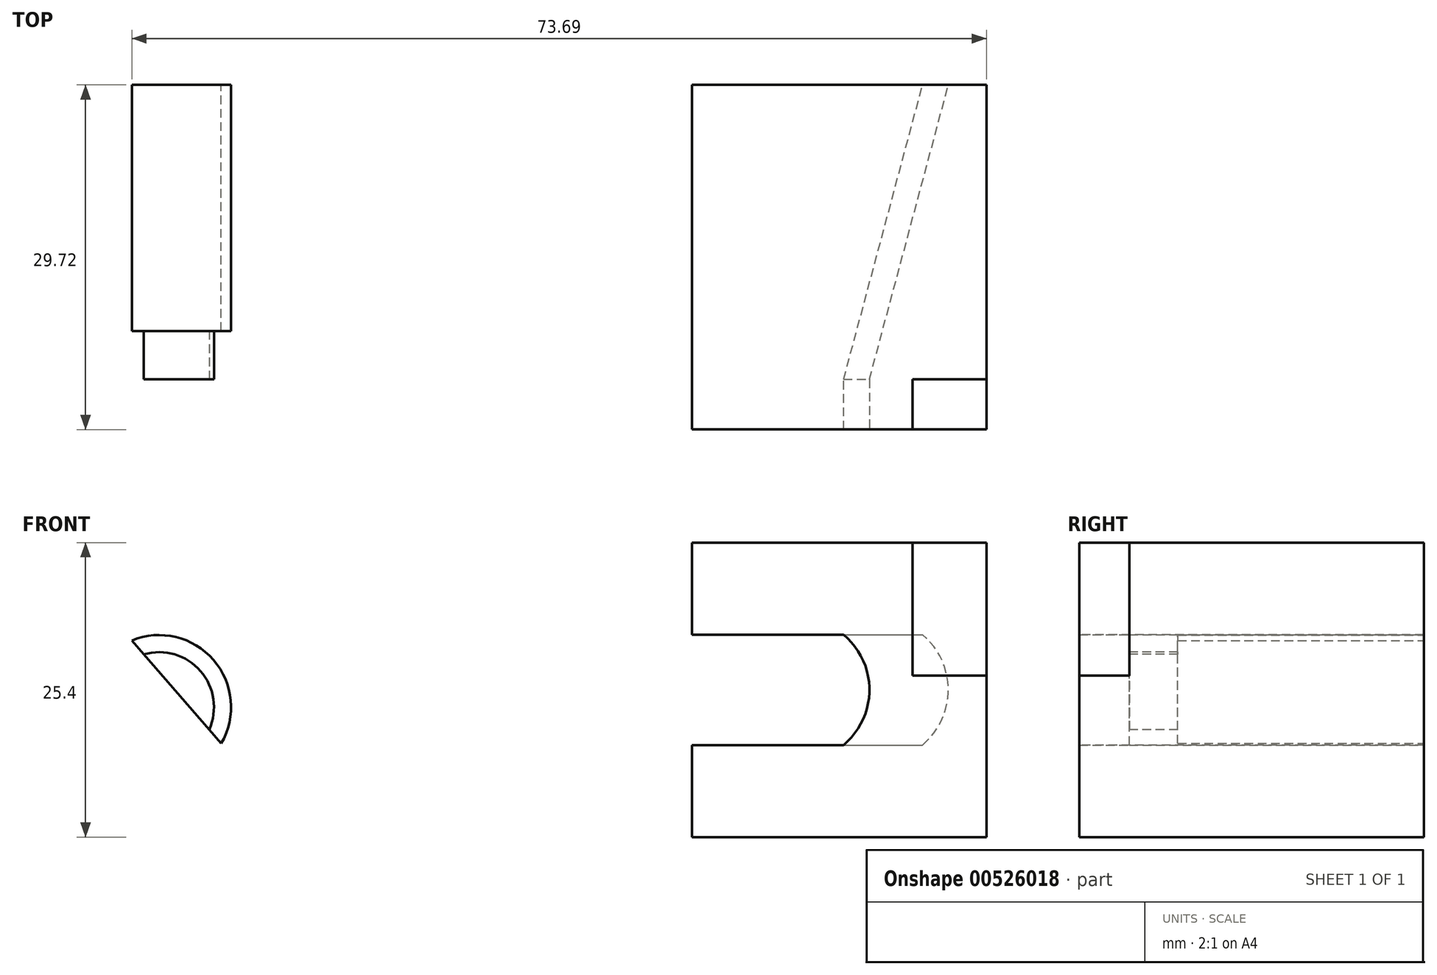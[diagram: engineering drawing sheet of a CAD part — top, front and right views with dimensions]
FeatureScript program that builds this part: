
annotation { "Feature Type Name" : "Feature", "Feature Type Description" : "" }
export const myFeature = defineFeature(function(context is Context, id is Id, definition is map)
    precondition{}
    {
        {
            var Q0;
            Q0=qCreatedBy(makeId("Front.planeOp"),FACE);
            var sketch = newSketch(context, id + "F0", { "sketchPlane" : qUnion([Q0])});
            skLineSegment(sketch, "E0.bottom", {"start": v(0, 0) * mm, "end": v(25.4, 0) * mm});
            skLineSegment(sketch, "E0.top", {"start": v(0, 25.4) * mm, "end": v(25.4, 25.4) * mm});
            skLineSegment(sketch, "E0.left", {"start": v(0, 0) * mm, "end": v(0, 25.4) * mm});
            skLineSegment(sketch, "E0.right", {"start": v(25.4, 0) * mm, "end": v(25.4, 25.4) * mm});
            skSolve(sketch);
        }
        {
            var Q0;
            Q0 = qSketchRegion(id + "F0", true);
            extrude(context, id + "F1", {"entities" : qUnion([Q0]), "depth" : 25.4 * mm, "offsetDistance" : 25.4 * mm});
        }
        {
            var Q0;
            Q0=makeQuery(id+"F1.opExtrude","CAP_EDGE",EDGE,{"disambiguationData":[OSD([sQuery(id+"F0.wireOp",EDGE,"E0.right")])],"isStart":true});
            cPlane(context, id + "F2", {"entities" : qUnion([Q0]), "cplaneType" : CPlaneType.LINE_ANGLE, "offset" : 25.4 * mm, "angle" : 75 * degree, "width" : 152.4 * mm, "height" : 152.4 * mm});
        }
        {
            var Q0;
            Q0=qCreatedBy(id+"F2.planeOp",FACE);
            var sketch = newSketch(context, id + "F3", { "sketchPlane" : qUnion([Q0])});
            skArc(sketch, "E1", {"start": v(-19.2, 17.46) * mm, "mid": v(-21.36, 12.7) * mm, "end": v(-19.2, 7.94) * mm});
            skLineSegment(sketch, "E2.0", {"start": v(-24.53, 0) * mm, "end": v(-24.53, 25.4) * mm, "construction": true});
            skLineSegment(sketch, "E3", {"start": v(-24.53, 12.7) * mm, "end": v(-15, 12.7) * mm, "construction": true});
            skLineSegment(sketch, "E4.0", {"start": v(0, 17.46) * mm, "end": v(0, 25.4) * mm, "construction": true});
            skLineSegment(sketch, "E5.bottom", {"start": v(-19.2, 7.94) * mm, "end": v(0, 7.94) * mm});
            skLineSegment(sketch, "E5.top", {"start": v(-19.2, 17.46) * mm, "end": v(0, 17.46) * mm});
            skLineSegment(sketch, "E5.left", {"start": v(-19.2, 7.94) * mm, "end": v(-19.2, 17.46) * mm, "construction": true});
            skLineSegment(sketch, "E5.right", {"start": v(0, 7.94) * mm, "end": v(0, 17.46) * mm});
            skLineSegment(sketch, "E6.0", {"start": v(0, 0) * mm, "end": v(0, 25.4) * mm, "construction": true});
            skArc(sketch, "E7", {"start": v(-19.2, 17.46) * mm, "mid": v(-8.66, 12.7) * mm, "end": v(-19.2, 7.94) * mm, "construction": true});
            skSolve(sketch);
        }
        {
            var Q0;
            Q0=makeQuery(id+"F3.imprint","IMPRINT",FACE,{"disambiguationData":[TD([[makeQuery(id+"F3.imprint","IMPRINT",EDGE,{"derivedFrom":sQuery(id+"F3.wireOp",EDGE,"E1")}),1.0]])]});
            extrude(context, id + "F4", {"entities" : qUnion([Q0]), "operationType" : NewBodyOperationType.REMOVE, "endBound" : BoundingType.THROUGH_ALL, "oppositeDirection" : true, "depth" : 25.4 * mm, "offsetDistance" : 25.4 * mm});
        }
        {
            var Q0;
            Q0=qCreatedBy(makeId("Front.planeOp"),FACE);
            var sketch = newSketch(context, id + "F5", { "sketchPlane" : qUnion([Q0])});
            skArc(sketch, "E8", {"start": v(-40.59, 8.07) * mm, "mid": v(-41.25, 15.28) * mm, "end": v(-48.3, 16.96) * mm});
            skLineSegment(sketch, "E9", {"start": v(-48.3, 16.96) * mm, "end": v(-40.59, 8.07) * mm});
            skSolve(sketch);
        }
        {
            var Q0;
            {var subQ0=sQuery(id+"F5.wireOp",EDGE,"E9");Q0=makeQuery(id+"F5.imprint","IMPRINT",FACE,{"disambiguationData":[TD([[makeQuery(id+"F5.imprint","IMPRINT",EDGE,{"derivedFrom":subQ0}),1.0]])]});}
            extrude(context, id + "F6", {"entities" : qUnion([Q0]), "depth" : 25.4 * mm, "offsetDistance" : 25.4 * mm});
        }
        {
            var Q0;
            Q0=makeQuery(id+"F6.opExtrude","CAP_EDGE",EDGE,{"disambiguationData":[OSD([sQuery(id+"F5.wireOp",EDGE,"E8")])],"isStart":false});
            cPlane(context, id + "F7", {"entities" : qUnion([Q0]), "cplaneType" : CPlaneType.LINE_ANGLE, "offset" : 25.4 * mm, "angle" : 0 * degree, "width" : 152.4 * mm, "height" : 152.4 * mm});
        }
        {
            var Q0;
            Q0=qCreatedBy(id+"F7.planeOp",FACE);
            var sketch = newSketch(context, id + "F8", { "sketchPlane" : qUnion([Q0])});
            skLineSegment(sketch, "E10", {"start": v(-39.74, 25.4) * mm, "end": v(-39.74, 0) * mm});
            skLineSegment(sketch, "E11", {"start": v(-39.74, 25.4) * mm, "end": v(-43.31, 25.4) * mm});
            skLineSegment(sketch, "E12.bottom", {"start": v(-39.74, 25.4) * mm, "end": v(-41.2, 25.4) * mm});
            skLineSegment(sketch, "E12.top", {"start": v(-39.74, 21.22) * mm, "end": v(-41.2, 21.22) * mm});
            skLineSegment(sketch, "E12.left", {"start": v(-39.74, 25.4) * mm, "end": v(-39.74, 21.22) * mm});
            skLineSegment(sketch, "E12.right", {"start": v(-41.2, 25.4) * mm, "end": v(-41.2, 21.22) * mm});
            skLineSegment(sketch, "E13.0", {"start": v(-48.3, 25.4) * mm, "end": v(-48.3, 0) * mm});
            skSolve(sketch);
        }
        {
            var Q0;
            Q0 = qSketchRegion(id + "F8", true);
            var Q1;
            Q1=makeQuery(id+"F6.opExtrude","SWEPT_FACE",FACE,{"disambiguationData":[OSD([sQuery(id+"F5.wireOp",EDGE,"E8")])]});
            revolve(context, id + "F9", {"operationType" : NewBodyOperationType.REMOVE, "entities" : qUnion([Q0]), "axis" : qUnion([Q1]), "revolveType" : RevolveType.FULL});
        }
        {
            var Q0;
            Q0=makeQuery(id+"F1.opExtrude","CAP_FACE",FACE,{"disambiguationData":[OSD([sQuery(id+"F0.wireOp",EDGE,"E0.bottom"),sQuery(id+"F0.wireOp",EDGE,"E0.top"),sQuery(id+"F0.wireOp",EDGE,"E0.left"),sQuery(id+"F0.wireOp",EDGE,"E0.right")])],"isStart":false});
            var sketch = newSketch(context, id + "F10", { "sketchPlane" : qUnion([Q0])});
            skLineSegment(sketch, "E14", {"start": v(19.01, 25.4) * mm, "end": v(19.01, 13.92) * mm});
            skLineSegment(sketch, "E15", {"start": v(19.01, 13.92) * mm, "end": v(25.4, 13.92) * mm});
            skPoint(sketch, "E16.0", {"position": v(25.4, 25.4) * mm});
            skLineSegment(sketch, "E17", {"start": v(25.4, 13.92) * mm, "end": v(25.4, 25.4) * mm});
            skLineSegment(sketch, "E18", {"start": v(19.01, 25.4) * mm, "end": v(25.4, 25.4) * mm});
            skSolve(sketch);
        }
        {
            var Q0;
            {var subQ12=sQuery(id+"F10.wireOp",EDGE,"E14");Q0=makeQuery(id+"F10.imprint","IMPRINT",FACE,{"disambiguationData":[TD([[makeQuery(id+"F10.imprint","IMPRINT",EDGE,{"derivedFrom":subQ12}),-1.0]])]});}
            extrude(context, id + "F11", {"entities" : qUnion([Q0]), "operationType" : NewBodyOperationType.ADD, "depth" : 4.32 * mm, "offsetDistance" : 25.4 * mm});
        }
    });
